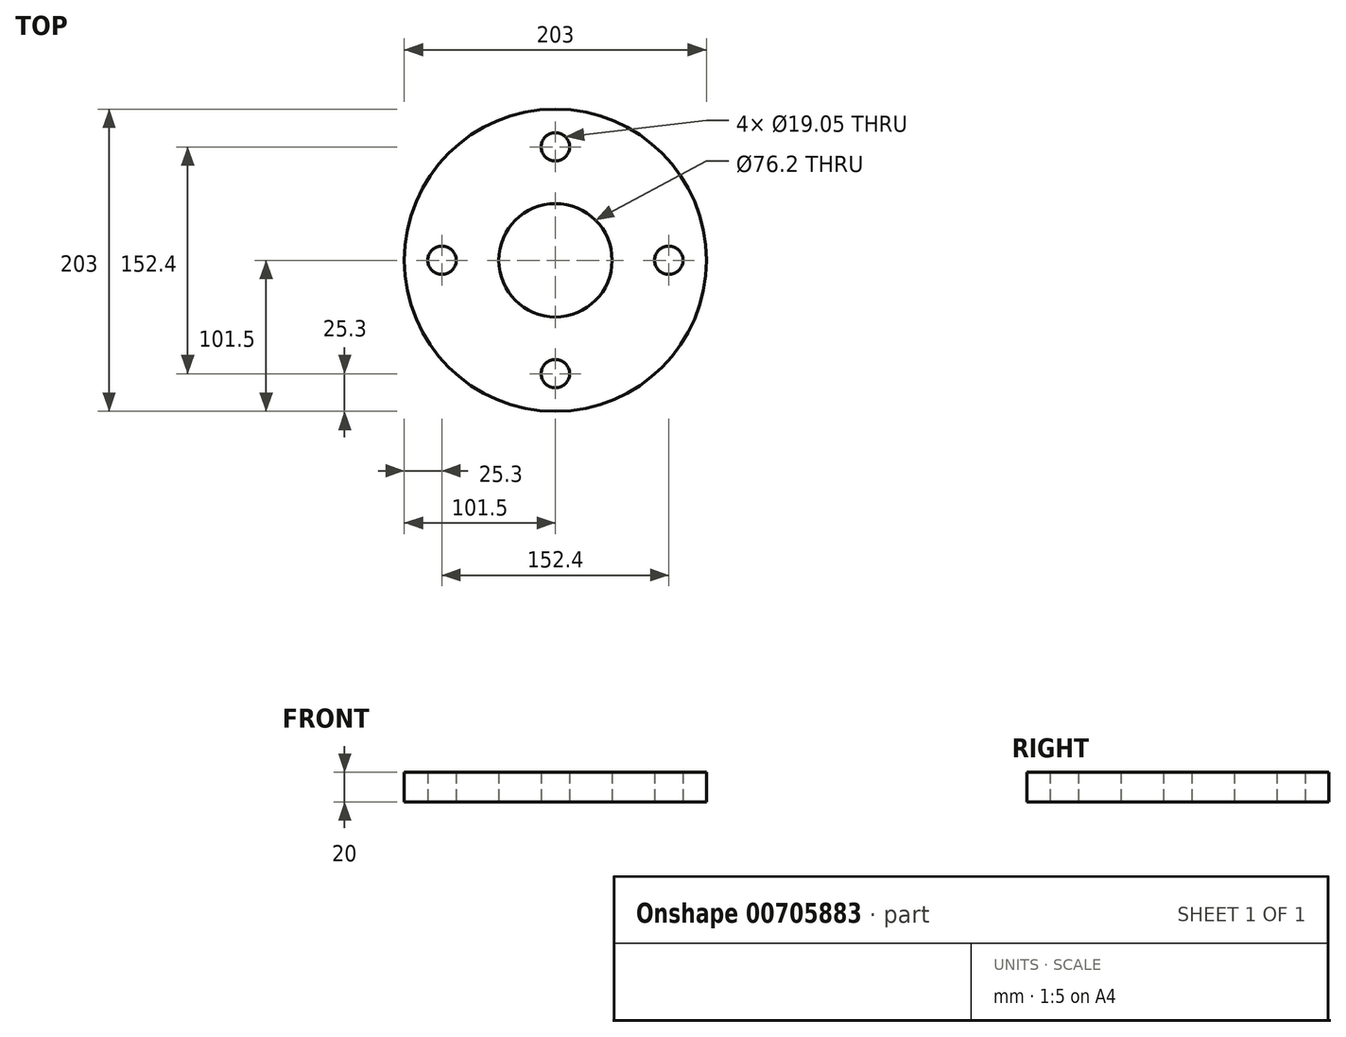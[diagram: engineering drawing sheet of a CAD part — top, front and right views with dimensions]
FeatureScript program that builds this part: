
annotation { "Feature Type Name" : "Feature", "Feature Type Description" : "" }
export const myFeature = defineFeature(function(context is Context, id is Id, definition is map)
    precondition{}
    {
        {
            var Q0;
            Q0=qCreatedBy(makeId("Top.planeOp"),FACE);
            var sketch = newSketch(context, id + "F0", { "sketchPlane" : qUnion([Q0])});
            skCircle(sketch, "E0", {"center": v(0, 0) * mm, "radius": 101.5 * mm});
            skCircle(sketch, "E1", {"center": v(0, 0) * mm, "radius": 76.2 * mm, "construction": true});
            skLineSegment(sketch, "E2", {"start": v(0, 101.5) * mm, "end": v(0, -101.5) * mm, "construction": true});
            skLineSegment(sketch, "E3", {"start": v(-101.5, 0) * mm, "end": v(101.5, 0) * mm, "construction": true});
            skCircle(sketch, "E4", {"center": v(-76.2, 0) * mm, "radius": 9.53 * mm});
            skCircle(sketch, "E5", {"center": v(0, 76.2) * mm, "radius": 9.53 * mm});
            skCircle(sketch, "E6", {"center": v(76.2, 0) * mm, "radius": 9.53 * mm});
            skCircle(sketch, "E7", {"center": v(0, -76.2) * mm, "radius": 9.53 * mm});
            skCircle(sketch, "E8", {"center": v(0, 0) * mm, "radius": 38.1 * mm});
            skSolve(sketch);
        }
        {
            var Q0;
            Q0 = qSketchRegion(id + "F0", true);
            extrude(context, id + "F1", {"entities" : qUnion([Q0]), "depth" : 20 * mm, "offsetDistance" : 25 * mm});
        }
    });
